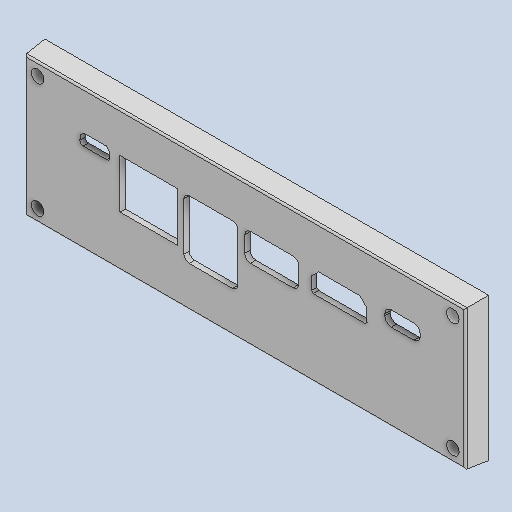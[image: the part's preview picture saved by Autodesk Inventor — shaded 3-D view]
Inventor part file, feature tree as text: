
AUTODESK INVENTOR PART (.ipt)
format: ipt  version: 2022.2 (Build 262287000, 287)  size: 285,696 bytes
history: native  units: mm
features: reference x20, other x5, extrude x4, sketch x4, chamfer x2, fillet x1, projected_geometry x1
ambient origin geometry x8: Origin, YZ Plane, XZ Plane, XY Plane, X Axis, Y Axis, Z Axis, Center Point
bodies: Solid1 (feature_tree)
feature tree (37):
  extrude  "Extrusion1"  Depth=0.5mm
  extrude  "Extrusion2"  Depth=6.0mm
  chamfer  "Chamfer1"  Distance=0.5mm
  chamfer  "Chamfer2"  Distance=0.5mm
  extrude  "Extrusion4"  TaperAngle=0.0deg  [1 undecoded]
  extrude  "Extrusion5"  Depth=0.5mm TaperAngle=45.0deg
  fillet  "Fillet1"  Radius=0.5mm
  sketch  "Sketch1"  dims[d0=6.0mm d1=-0.872665mm d2=0.5mm]
  reference  "Reference1"
  reference  "Reference2"
  sketch  "Sketch2"  dims[d3=15.5mm d4=6.0mm]
  reference  "Reference13"
  reference  "Reference14"
  reference  "Reference15"
  reference  "Reference16"
  reference  "Reference17"
  reference  "Reference18"
  reference  "Reference19"
  reference  "Reference20"
  reference  "Reference21"
  reference  "Reference22"
  reference  "Reference23"
  reference  "Reference24"
  sketch  "Sketch4"  dims[d5=1.0mm]
  projected_geometry  "Projected Loop2"
  sketch  "Sketch5"  dims[d6=1.0mm d7=0.5mm d8=0.5mm d9=0.0mm d10=0.0mm d11=2.0mm d12=2.0mm d13=45.0deg d14=0.5mm d15=2.0mm d16=45.0deg d21=4.5mm d22=-4.363323mm d26=0.0mm d27=0.0mm d28=0.5mm]
  reference  "Reference25"
  reference  "Reference26"
  reference  "Reference27"
  reference  "Reference28"
  reference  "Reference29"
  reference  "Reference30"
  other  "<userpath>\Desktop\Jetson-Nano-2GB-Case\A.iam"
  other  "A.iam"
  other  "A-02:1"
  other  "A-01:1"
  other  "A-00:2"
note: 1 required parameter value undecoded (feature->parameter linkage not recoverable at this tier; creation-order binding heuristic only, values carry confidence <= 0.55)
